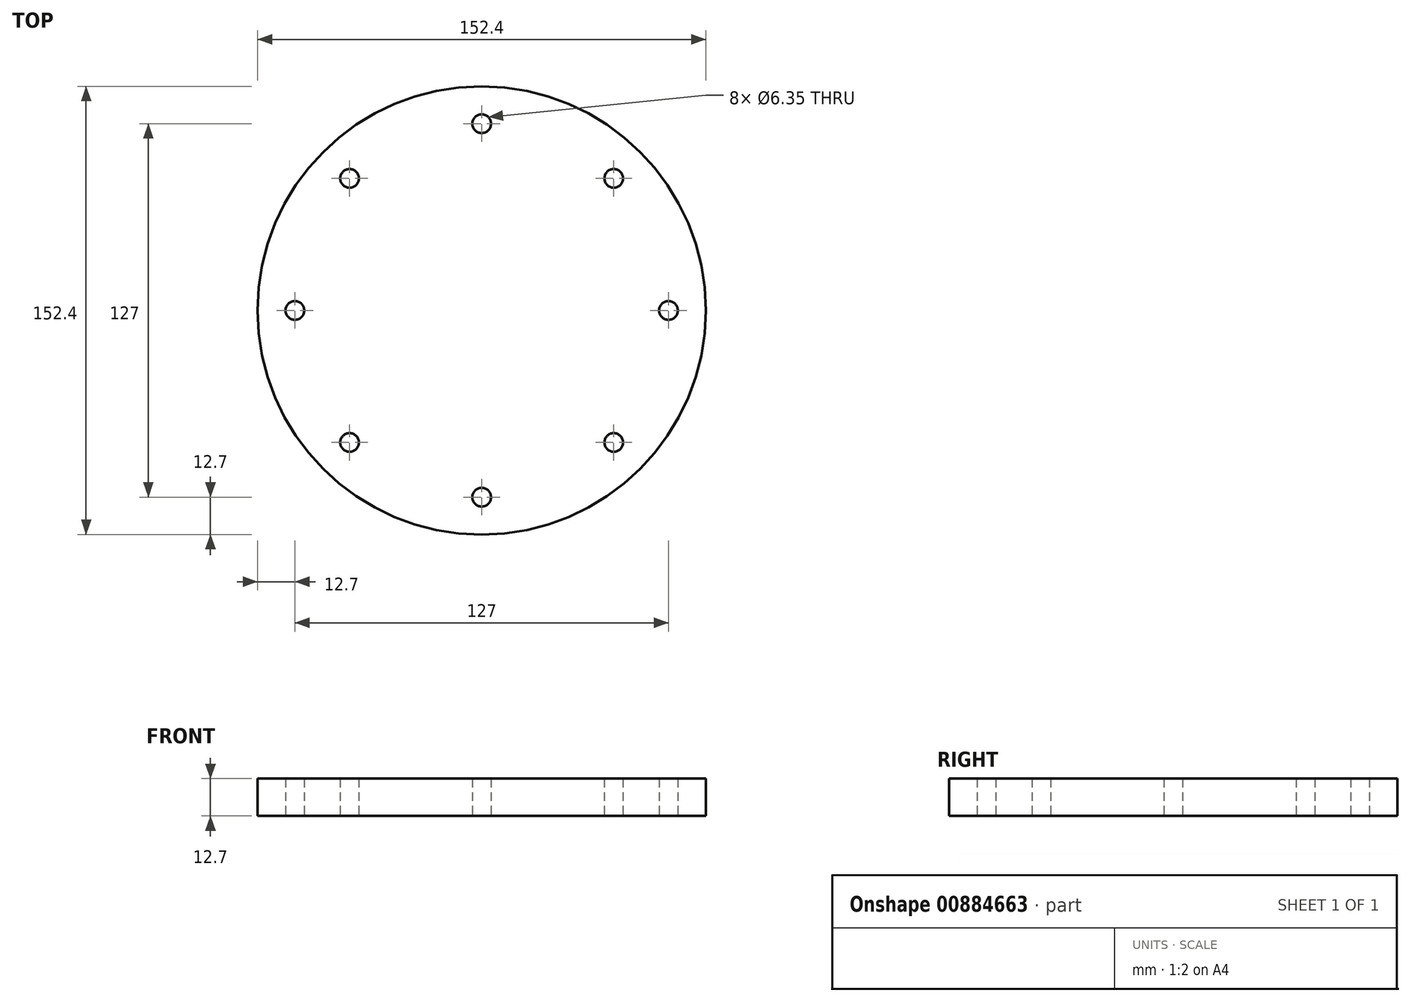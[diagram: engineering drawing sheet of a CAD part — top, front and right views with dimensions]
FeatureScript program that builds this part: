
annotation { "Feature Type Name" : "Feature", "Feature Type Description" : "" }
export const myFeature = defineFeature(function(context is Context, id is Id, definition is map)
    precondition{}
    {
        {
            var Q0;
            Q0=qCreatedBy(makeId("Top.planeOp"),FACE);
            var sketch = newSketch(context, id + "F0", { "sketchPlane" : qUnion([Q0])});
            skCircle(sketch, "E0", {"center": v(0, 0) * mm, "radius": 76.2 * mm});
            skCircle(sketch, "E1", {"center": v(0, 0) * mm, "radius": 63.5 * mm});
            skLineSegment(sketch, "E2", {"start": v(0, 0) * mm, "end": v(-44.9, 44.9) * mm});
            skLineSegment(sketch, "E3", {"start": v(0, 0) * mm, "end": v(44.9, 44.9) * mm});
            skLineSegment(sketch, "E4", {"start": v(0, 0) * mm, "end": v(-44.9, -44.9) * mm});
            skLineSegment(sketch, "E5", {"start": v(0, 0) * mm, "end": v(44.9, -44.9) * mm});
            skCircle(sketch, "E6", {"center": v(-44.9, 44.9) * mm, "radius": 3.18 * mm});
            skCircle(sketch, "E7", {"center": v(-63.5, 0) * mm, "radius": 3.18 * mm});
            skCircle(sketch, "E8", {"center": v(-44.9, -44.9) * mm, "radius": 3.18 * mm});
            skCircle(sketch, "E9", {"center": v(0, -63.5) * mm, "radius": 3.18 * mm});
            skCircle(sketch, "E10", {"center": v(44.9, -44.9) * mm, "radius": 3.18 * mm});
            skCircle(sketch, "E11", {"center": v(63.5, 0) * mm, "radius": 3.18 * mm});
            skCircle(sketch, "E12", {"center": v(44.9, 44.9) * mm, "radius": 3.18 * mm});
            skCircle(sketch, "E13", {"center": v(0, 63.5) * mm, "radius": 3.18 * mm});
            skSolve(sketch);
        }
        {
            var Q0;
            Q0 = qSketchRegion(id + "F0", true);
            var Q1;
            {var subQ5=sQuery(id+"F0.wireOp",EDGE,"E6");var subQ8=sQuery(id+"F0.wireOp",EDGE,"E1");var subQ12=makeQuery(id+"F0.imprint","INTERSECT",VERTEX,{"disambiguationData":[OD(1.0)],"derivedFrom":[subQ8,subQ5]});Q1=makeQuery(id+"F0.imprint","IMPRINT",FACE,{"disambiguationData":[TD([[makeQuery(id+"F0.imprint","IMPRINT",EDGE,{"disambiguationData":[TD([[subQ12,-1.0]])],"derivedFrom":subQ8}),1.0]])]});}
            var Q2;
            {var subQ6=sQuery(id+"F0.wireOp",EDGE,"E1");var subQ9=sQuery(id+"F0.wireOp",EDGE,"E8");var subQ11=makeQuery(id+"F0.imprint","INTERSECT",VERTEX,{"disambiguationData":[OD(1.0)],"derivedFrom":[subQ6,subQ9]});Q2=makeQuery(id+"F0.imprint","IMPRINT",FACE,{"disambiguationData":[TD([[makeQuery(id+"F0.imprint","IMPRINT",EDGE,{"disambiguationData":[TD([[subQ11,-1.0]])],"derivedFrom":subQ6}),1.0]])]});}
            var Q3;
            {var subQ5=sQuery(id+"F0.wireOp",EDGE,"E12");var subQ7=sQuery(id+"F0.wireOp",EDGE,"E1");var subQ8=makeQuery(id+"F0.imprint","INTERSECT",VERTEX,{"disambiguationData":[OD(0.0)],"derivedFrom":[subQ7,subQ5]});Q3=makeQuery(id+"F0.imprint","IMPRINT",FACE,{"disambiguationData":[TD([[makeQuery(id+"F0.imprint","IMPRINT",EDGE,{"disambiguationData":[TD([[subQ8,1.0]])],"derivedFrom":subQ7}),1.0]])]});}
            var Q4;
            {var subQ3=sQuery(id+"F0.wireOp",EDGE,"E12");var subQ8=sQuery(id+"F0.wireOp",EDGE,"E1");var subQ11=makeQuery(id+"F0.imprint","INTERSECT",VERTEX,{"disambiguationData":[OD(1.0)],"derivedFrom":[subQ8,subQ3]});Q4=makeQuery(id+"F0.imprint","IMPRINT",FACE,{"disambiguationData":[TD([[makeQuery(id+"F0.imprint","IMPRINT",EDGE,{"disambiguationData":[TD([[subQ11,-1.0]])],"derivedFrom":subQ8}),1.0]])]});}
            extrude(context, id + "F1", {"entities" : qUnion([Q0, Q1, Q2, Q3, Q4]), "depth" : 12.7 * mm, "offsetDistance" : 25.4 * mm});
        }
    });
